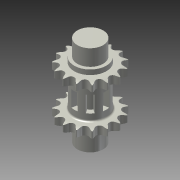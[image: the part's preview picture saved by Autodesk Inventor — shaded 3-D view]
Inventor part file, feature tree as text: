
AUTODESK INVENTOR PART (.ipt)
format: ipt  version: 2015 (Build 190159000, 159)  size: 786,944 bytes
history: native  units: mm
features: other x7, sketch x4, imported_body x1, hole x1
ambient origin geometry x8: Origin, YZ Plane, XZ Plane, XY Plane, X Axis, Y Axis, Z Axis, Center Point
bodies: Body1 (feature_tree)
feature tree (13):
  other  "sprocket_encoder_axis_left_2.ipt"
  other  "Sólido3::sprocket_encoder_axis_left_2.ipt"
  other  "OperaciónIdentificador1"
  imported_body  "Base"
  other  "Tooth_drawing"
  other  "Canal_drawing"
  other  "Axis_drawing"
  hole  "Holes_drawing"  [1 undecoded]
  sketch  "Boceto9"
  sketch  "Boceto10"
  sketch  "Boceto8"  dims[d0=10.0mm]
  sketch  "Boceto11"
  other  "Sólido1"
note: 1 required parameter value undecoded (feature->parameter linkage not recoverable at this tier; creation-order binding heuristic only, values carry confidence <= 0.55)
